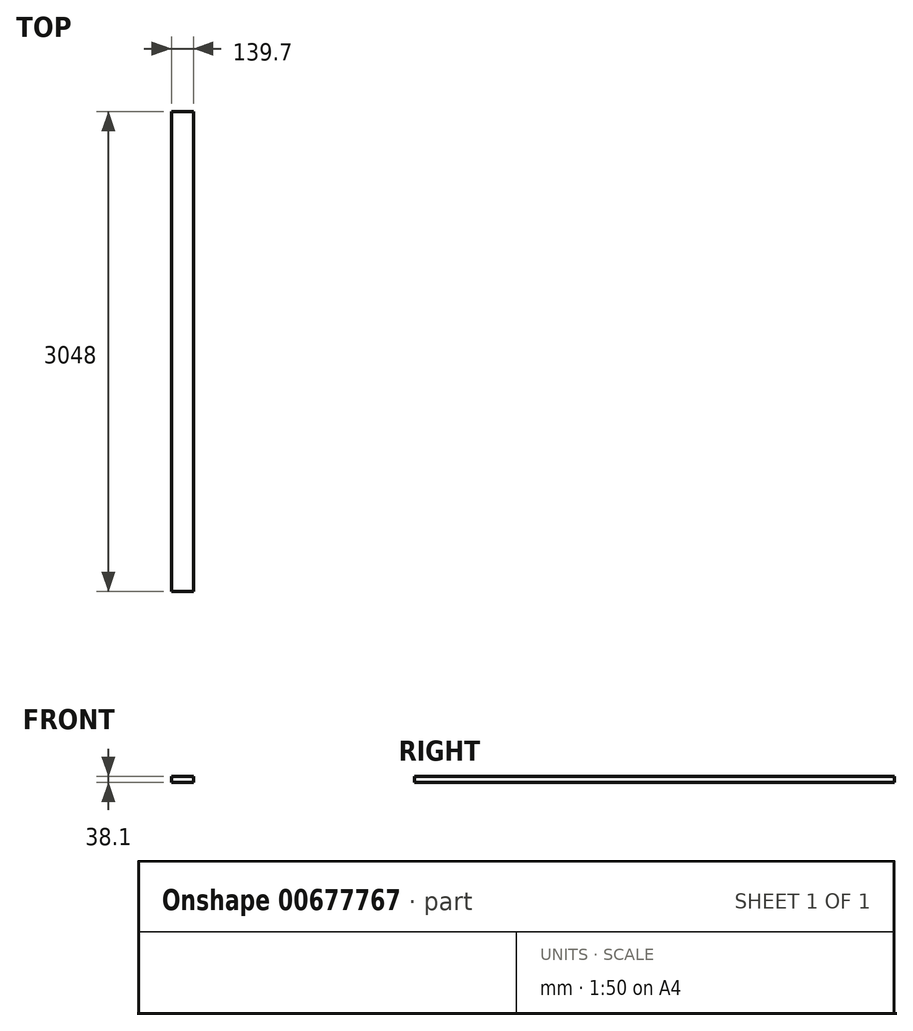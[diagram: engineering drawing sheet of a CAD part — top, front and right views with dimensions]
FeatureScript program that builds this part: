
annotation { "Feature Type Name" : "Feature", "Feature Type Description" : "" }
export const myFeature = defineFeature(function(context is Context, id is Id, definition is map)
    precondition{}
    {
        {
            var Q0;
            Q0=qCreatedBy(makeId("Front.planeOp"),FACE);
            var sketch = newSketch(context, id + "F0", { "sketchPlane" : qUnion([Q0])});
            skLineSegment(sketch, "E0.bottom", {"start": v(-341.97, -77.25) * mm, "end": v(-202.27, -77.25) * mm});
            skLineSegment(sketch, "E0.top", {"start": v(-341.97, -115.35) * mm, "end": v(-202.27, -115.35) * mm});
            skLineSegment(sketch, "E0.left", {"start": v(-341.97, -77.25) * mm, "end": v(-341.97, -115.35) * mm});
            skLineSegment(sketch, "E0.right", {"start": v(-202.27, -77.25) * mm, "end": v(-202.27, -115.35) * mm});
            skSolve(sketch);
        }
        {
            var Q0;
            Q0=makeQuery(id+"F0.imprint","IMPRINT",FACE,{"disambiguationData":[TD([[makeQuery(id+"F0.imprint","IMPRINT",EDGE,{"derivedFrom":sQuery(id+"F0.wireOp",EDGE,"E0.bottom")}),-1.0]])]});
            extrude(context, id + "F1", {"entities" : qUnion([Q0]), "depth" : 3048 * mm, "offsetDistance" : 25.4 * mm});
        }
    });
